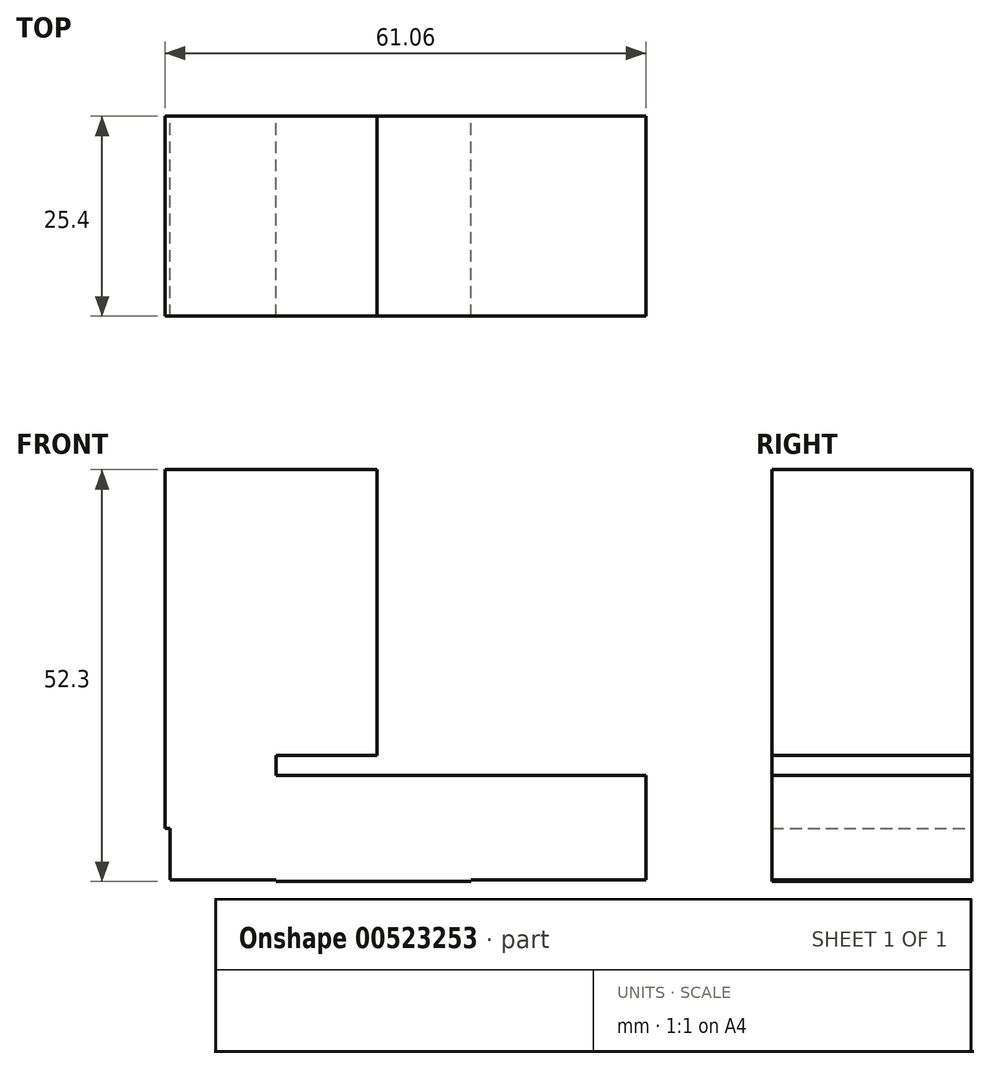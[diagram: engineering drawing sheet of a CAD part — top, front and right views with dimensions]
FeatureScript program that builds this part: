
annotation { "Feature Type Name" : "Feature", "Feature Type Description" : "" }
export const myFeature = defineFeature(function(context is Context, id is Id, definition is map)
    precondition{}
    {
        {
            var Q0;
            Q0=qCreatedBy(makeId("Front.planeOp"),FACE);
            var sketch = newSketch(context, id + "F0", { "sketchPlane" : qUnion([Q0])});
            skLineSegment(sketch, "E0.bottom", {"start": v(-38.2, 13.3) * mm, "end": v(22.23, 13.3) * mm});
            skLineSegment(sketch, "E0.top", {"start": v(-38.2, 0) * mm, "end": v(22.23, 0) * mm});
            skLineSegment(sketch, "E0.left", {"start": v(-38.2, 13.3) * mm, "end": v(-38.2, 0) * mm});
            skLineSegment(sketch, "E0.right", {"start": v(22.23, 13.3) * mm, "end": v(22.23, 0) * mm});
            skLineSegment(sketch, "E1.bottom", {"start": v(0, -0.16) * mm, "end": v(-24.74, -0.16) * mm});
            skLineSegment(sketch, "E1.top", {"start": v(0, 13.3) * mm, "end": v(-24.74, 13.3) * mm});
            skLineSegment(sketch, "E1.left", {"start": v(0, -0.16) * mm, "end": v(0, 13.3) * mm});
            skLineSegment(sketch, "E1.right", {"start": v(-24.74, -0.16) * mm, "end": v(-24.74, 13.3) * mm});
            skLineSegment(sketch, "E2.bottom", {"start": v(-24.74, 6.58) * mm, "end": v(-38.83, 6.58) * mm});
            skLineSegment(sketch, "E2.top", {"start": v(-24.74, 15.81) * mm, "end": v(-38.83, 15.81) * mm});
            skLineSegment(sketch, "E2.left", {"start": v(-24.74, 6.58) * mm, "end": v(-24.74, 15.81) * mm});
            skLineSegment(sketch, "E2.right", {"start": v(-38.83, 6.58) * mm, "end": v(-38.83, 15.81) * mm});
            skLineSegment(sketch, "E3.bottom", {"start": v(-38.83, 15.81) * mm, "end": v(-11.9, 15.81) * mm});
            skLineSegment(sketch, "E3.top", {"start": v(-38.83, 52.14) * mm, "end": v(-11.9, 52.14) * mm});
            skLineSegment(sketch, "E3.left", {"start": v(-38.83, 15.81) * mm, "end": v(-38.83, 52.14) * mm});
            skLineSegment(sketch, "E3.right", {"start": v(-11.9, 15.81) * mm, "end": v(-11.9, 52.14) * mm});
            skSolve(sketch);
        }
        {
            var Q0;
            Q0 = qSketchRegion(id + "F0", true);
            extrude(context, id + "F1", {"entities" : qUnion([Q0]), "depth" : 25.4 * mm, "offsetDistance" : 25.4 * mm});
        }
    });
